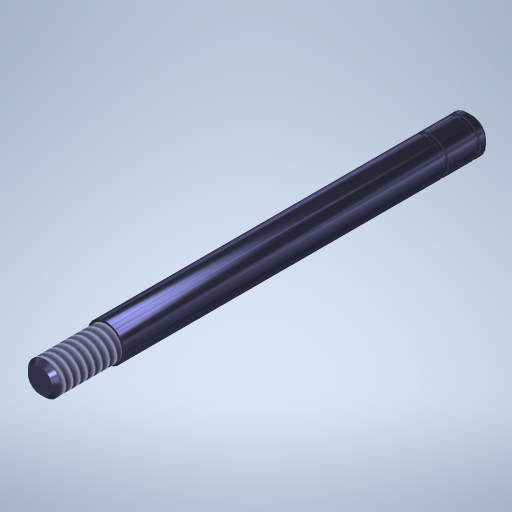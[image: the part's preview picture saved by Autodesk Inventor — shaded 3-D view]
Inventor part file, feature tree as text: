
AUTODESK INVENTOR PART (.ipt)
format: ipt  version: 2023.1 (Build 271208000, 208)  size: 309,760 bytes
history: native  units: in
note: dims shown in document units (in); Inventor stores cm internally (conversion verified against a paired STEP export)
features: extrude x4, sketch x4, plane x2, chamfer x1, thread x1
ambient origin geometry x8: Origin, YZ Plane, XZ Plane, XY Plane, X Axis, Y Axis, Z Axis, Center Point
bodies: Solid1 (feature_tree)
feature tree (12):
  extrude  "Extrusion1"  Depth=1.25in TaperAngle=0.0deg
  extrude  "Extrusion2"  Depth=0.225in TaperAngle=0.0deg
  plane  "Work Plane1"
  extrude  "Extrusion3"  Depth=0.015in TaperAngle=0.0deg
  plane  "Work Plane2"
  extrude  "Extrusion4"  Depth=0.015in TaperAngle=0.0deg
  chamfer  "Chamfer1"  Distance=0.015in Angle=45.0deg
  thread  "Thread1"  [1 undecoded]
  sketch  "Sketch1"  dims[d0=0.125in d1=1.25in d2=0.0in]
  sketch  "Sketch2"  dims[d3=0.112in d4=0.225in d5=0.0in]
  sketch  "Sketch3"  dims[d6=-0.032in d7=0.015in d8=0.0in]
  sketch  "Sketch4"  dims[d9=-0.0938in d10=0.015in d11=0.0in d12=0.015in d13=0.125in d14=45.0deg d15=1.0in d16=0.0in]
note: 1 required parameter value undecoded (feature->parameter linkage not recoverable at this tier; creation-order binding heuristic only, values carry confidence <= 0.55)
